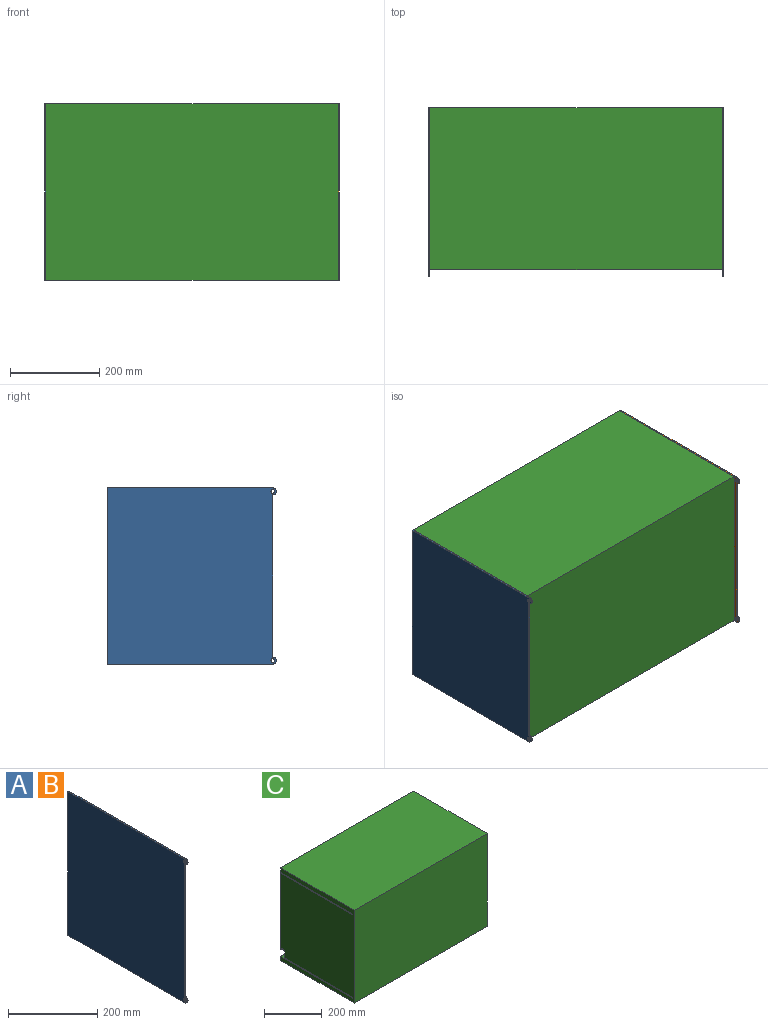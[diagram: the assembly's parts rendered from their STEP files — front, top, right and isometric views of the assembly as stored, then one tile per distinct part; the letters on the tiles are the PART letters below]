
ASSEMBLY  parts=3 mates=2
PART A: 10 faces, bbox 3.2x377.4x394.5 mm
  f0: cylinder r=7.87mm len=15.75mm, axis (-1,0,0), area 78.5mm2, adj f1,f7,f8,f9
  f1: plane 362.99x3.18mm, normal (0,-1,0), area 1152.5mm2, adj f0,f2,f8,f9
  f2: cylinder r=7.87mm len=15.75mm, axis (-1,0,0), area 78.5mm2, adj f1,f3,f8,f9
  f3: plane 369.49x3.18mm, normal (0,0,-1), area 1173.1mm2, adj f2,f4,f8,f9
  f4: plane 394.49x3.18mm, normal (0,1,0), area 1252.5mm2, adj f3,f7,f8,f9
  f5: cylinder r=4mm len=8mm, axis (-1,0,0), area 79.8mm2, adj f8,f9
  f6: cylinder r=4mm len=8mm, axis (-1,0,0), area 79.8mm2, adj f8,f9
  f7: plane 369.49x3.18mm, normal (0,0,1), area 1173.1mm2, adj f0,f4,f8,f9
  f8: plane 394.49x377.37mm, normal (1,0,0), area 145854.9mm2, adj f0,f1,f2,f3,f4,f5,f6,f7
  f9: plane 394.49x377.37mm, normal (-1,0,0), area 145854.9mm2, adj f0,f1,f2,f3,f4,f5,f6,f7
PART B: same geometry as A
PART C: 17 faces, bbox 654.1x362x394.5 mm
  f0: plane 654.05x17.9mm, normal (0,1,0), area 11707.7mm2, adj f2,f3,f7,f14
  f1: plane 654.05x325.84mm, normal (0,1,0), area 213114.3mm2, adj f2,f3,f10,f11
  f2: plane 394.49x361.95mm, normal (-1,0,0), area 139939.3mm2, adj f0,f1,f4,f5,f6,f7,f8,f9
  f3: plane 394.49x361.95mm, normal (1,0,0), area 139939.3mm2, adj f0,f1,f4,f5,f6,f7,f8,f9
  f4: plane 654.05x394.49mm, normal (0,-1,0), area 258014.5mm2, adj f2,f3,f5,f7
  f5: plane 654.05x361.95mm, normal (0,0,1), area 236733.4mm2, adj f2,f3,f4,f6
  f6: plane 654.05x19mm, normal (0,1,0), area 12426.4mm2, adj f2,f3,f5,f12
  f7: plane 654.05x361.95mm, normal (0,0,-1), area 236733.4mm2, adj f0,f2,f3,f4
  f8: plane 654.05x25.4mm, normal (0,1,0), area 16612.9mm2, adj f2,f3,f9,f15
  f9: cylinder r=8.12mm len=654.05mm, axis (-1,0,0), area 16675.4mm2, adj f2,f3,f8,f10
  f10: plane 654.05x2.82mm, normal (0,0,-1), area 1843.7mm2, adj f1,f2,f3,f9
  f11: plane 654.05x355.6mm, normal (0,0,1), area 232580.2mm2, adj f1,f2,f3,f13
  f12: plane 654.05x355.6mm, normal (0,0,-1), area 232580.2mm2, adj f2,f3,f6,f13
  f13: plane 654.05x3.18mm, normal (0,1,0), area 2076.6mm2, adj f2,f3,f11,f12
  f14: plane 654.05x355.6mm, normal (0,0,1), area 232580.2mm2, adj f0,f2,f3,f16
  f15: plane 654.05x336.55mm, normal (0,0,-1), area 220120.5mm2, adj f2,f3,f8,f16
  f16: plane 654.05x3.18mm, normal (0,1,0), area 2076.6mm2, adj f2,f3,f14,f15
PLACE A t=(-4101.11,5059.98,-4397.8)mm
PLACE B t=(-3443.89,5059.98,-4397.8)mm
PLACE C t=(-2168.39,5059.98,-931.28)mm
MATE fastened B.f9 <-> C.f3  axis (-1,0,0) through (-3443.89,-3105.52,-1466.79)mm
MATE fastened A.f8 <-> C.f2  axis (1,0,0) through (-4097.94,-3105.52,-1466.79)mm
